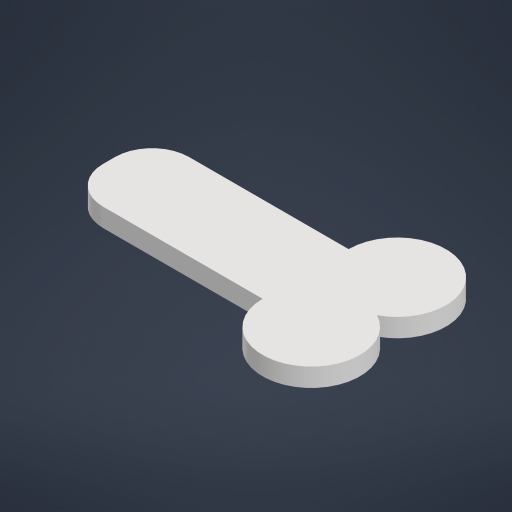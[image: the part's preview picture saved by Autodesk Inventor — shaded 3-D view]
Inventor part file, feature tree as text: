
AUTODESK INVENTOR PART (.ipt)
format: ipt  version: 2023 (Build 270158000, 158)  size: 172,032 bytes
history: native  units: in
note: dims shown in document units (in); Inventor stores cm internally (conversion verified against a paired STEP export)
features: extrude x1, fillet x1, sketch x1
ambient origin geometry x8: Origin, YZ Plane, XZ Plane, XY Plane, X Axis, Y Axis, Z Axis, Center Point
bodies: Solid1 (feature_tree)
feature tree (3):
  extrude  "Extrusion1"  Depth=0.1in
  fillet  "Fillet1"  [1 undecoded]
  sketch  "Sketch1"  dims[d0=0.05in d1=0.0in d2=0.1in]
note: 1 required parameter value undecoded (feature->parameter linkage not recoverable at this tier; creation-order binding heuristic only, values carry confidence <= 0.55)
